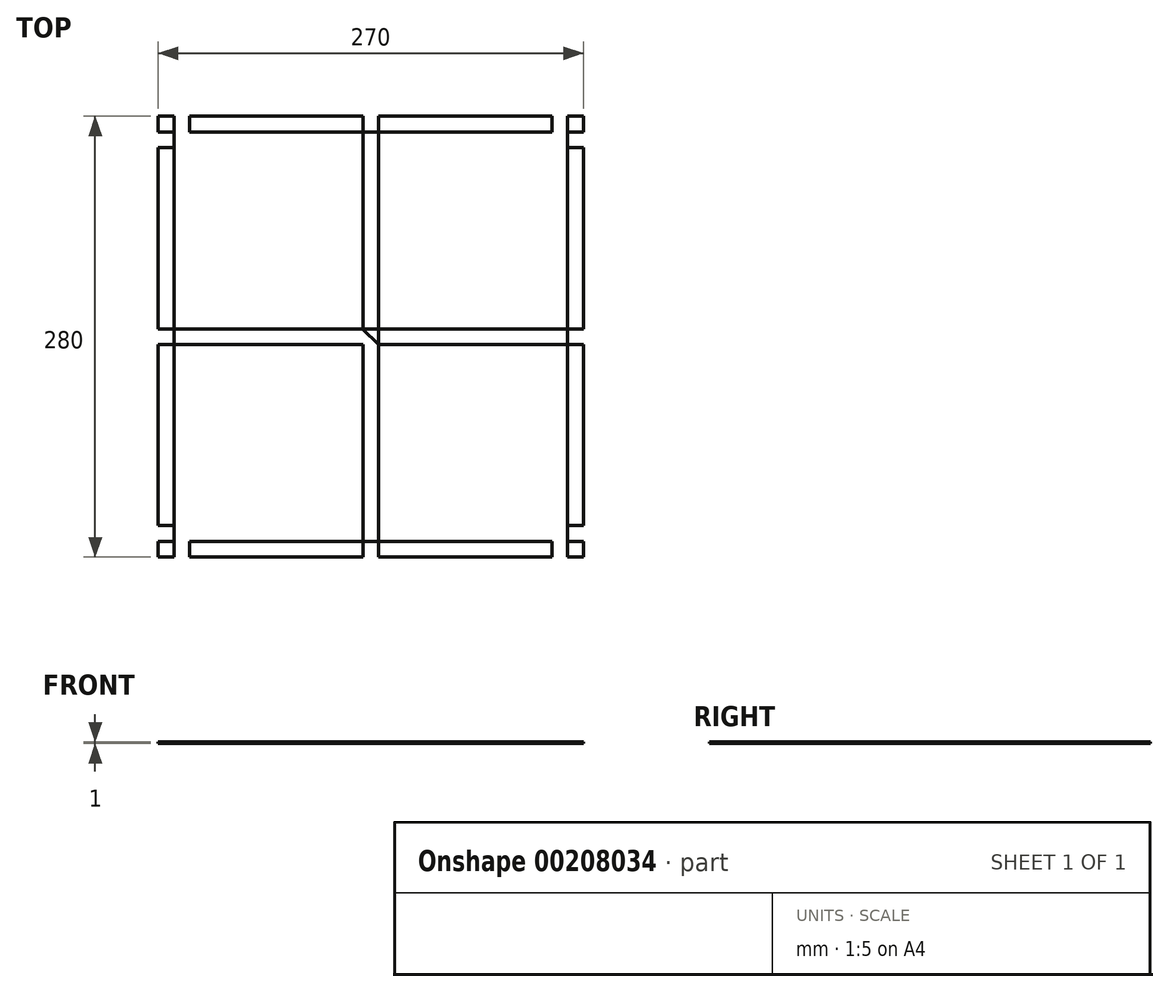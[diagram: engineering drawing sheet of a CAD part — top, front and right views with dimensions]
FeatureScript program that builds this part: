
annotation { "Feature Type Name" : "Feature", "Feature Type Description" : "" }
export const myFeature = defineFeature(function(context is Context, id is Id, definition is map)
    precondition{}
    {
        {
            var Q0;
            Q0=qCreatedBy(makeId("Top.planeOp"),FACE);
            var sketch = newSketch(context, id + "F0", { "sketchPlane" : qUnion([Q0])});
            skLineSegment(sketch, "E0.bottom", {"start": v(-135, 140) * mm, "end": v(135, 140) * mm});
            skLineSegment(sketch, "E0.top", {"start": v(-135, -140) * mm, "end": v(135, -140) * mm});
            skLineSegment(sketch, "E0.left", {"start": v(-135, 140) * mm, "end": v(-135, -140) * mm});
            skLineSegment(sketch, "E0.right", {"start": v(135, 140) * mm, "end": v(135, -140) * mm});
            skSolve(sketch);
        }
        {
            var Q0;
            Q0=makeQuery(id+"F0.imprint","IMPRINT",FACE,{"disambiguationData":[TD([[makeQuery(id+"F0.imprint","IMPRINT",EDGE,{"derivedFrom":sQuery(id+"F0.wireOp",EDGE,"E0.bottom")}),-1.0]])]});
            extrude(context, id + "F1", {"entities" : qUnion([Q0]), "depth" : 1 * mm});
        }
        {
            var Q0;
            Q0=makeQuery(id+"F1.opExtrude","CAP_FACE",FACE,{"disambiguationData":[OSD([sQuery(id+"F0.wireOp",EDGE,"E0.bottom"),sQuery(id+"F0.wireOp",EDGE,"E0.top"),sQuery(id+"F0.wireOp",EDGE,"E0.left"),sQuery(id+"F0.wireOp",EDGE,"E0.right")])],"isStart":false});
            var sketch = newSketch(context, id + "F2", { "sketchPlane" : qUnion([Q0])});
            skLineSegment(sketch, "E1.bottom", {"start": v(-125, 130) * mm, "end": v(-5, 130) * mm});
            skLineSegment(sketch, "E1.top", {"start": v(-125, 5) * mm, "end": v(-5, 5) * mm});
            skLineSegment(sketch, "E1.left", {"start": v(-125, 130) * mm, "end": v(-125, 5) * mm});
            skLineSegment(sketch, "E1.right", {"start": v(-5, 130) * mm, "end": v(-5, 5) * mm});
            skLineSegment(sketch, "E2.bottom", {"start": v(5, 130) * mm, "end": v(125, 130) * mm});
            skLineSegment(sketch, "E2.top", {"start": v(5, 5) * mm, "end": v(125, 5) * mm});
            skLineSegment(sketch, "E2.left", {"start": v(5, 130) * mm, "end": v(5, 5) * mm});
            skLineSegment(sketch, "E2.right", {"start": v(125, 130) * mm, "end": v(125, 5) * mm});
            skLineSegment(sketch, "E3.bottom", {"start": v(-125, -5) * mm, "end": v(-5, -5) * mm});
            skLineSegment(sketch, "E3.top", {"start": v(-125, -130) * mm, "end": v(-5, -130) * mm});
            skLineSegment(sketch, "E3.left", {"start": v(-125, -5) * mm, "end": v(-125, -130) * mm});
            skLineSegment(sketch, "E3.right", {"start": v(-5, -5) * mm, "end": v(-5, -130) * mm});
            skLineSegment(sketch, "E4.bottom", {"start": v(5, -5) * mm, "end": v(125, -5) * mm});
            skLineSegment(sketch, "E4.top", {"start": v(5, -130) * mm, "end": v(125, -130) * mm});
            skLineSegment(sketch, "E4.left", {"start": v(5, -5) * mm, "end": v(5, -130) * mm});
            skLineSegment(sketch, "E4.right", {"start": v(125, -5) * mm, "end": v(125, -130) * mm});
            skSolve(sketch);
        }
        {
            var Q0;
            Q0=makeQuery(id+"F2.imprint","IMPRINT",FACE,{"disambiguationData":[TD([[makeQuery(id+"F2.imprint","IMPRINT",EDGE,{"derivedFrom":sQuery(id+"F2.wireOp",EDGE,"E1.bottom")}),-1.0]])]});
            var Q1;
            Q1=makeQuery(id+"F2.imprint","IMPRINT",FACE,{"disambiguationData":[TD([[makeQuery(id+"F2.imprint","IMPRINT",EDGE,{"derivedFrom":sQuery(id+"F2.wireOp",EDGE,"E2.bottom")}),-1.0]])]});
            var Q2;
            Q2=makeQuery(id+"F2.imprint","IMPRINT",FACE,{"disambiguationData":[TD([[makeQuery(id+"F2.imprint","IMPRINT",EDGE,{"derivedFrom":sQuery(id+"F2.wireOp",EDGE,"E4.bottom")}),-1.0]])]});
            var Q3;
            Q3=makeQuery(id+"F2.imprint","IMPRINT",FACE,{"disambiguationData":[TD([[makeQuery(id+"F2.imprint","IMPRINT",EDGE,{"derivedFrom":sQuery(id+"F2.wireOp",EDGE,"E3.bottom")}),-1.0]])]});
            extrude(context, id + "F3", {"entities" : qUnion([Q0, Q1, Q2, Q3]), "operationType" : NewBodyOperationType.REMOVE, "endBound" : BoundingType.THROUGH_ALL, "oppositeDirection" : true, "depth" : 25 * mm});
        }
        {
            var Q0;
            Q0=makeQuery(id+"F2.imprint","IMPRINT",FACE,{"disambiguationData":[TD([[makeQuery(id+"F2.imprint","IMPRINT",EDGE,{"derivedFrom":sQuery(id+"F2.wireOp",EDGE,"E1.bottom")}),1.0]])]});
            var sketch = newSketch(context, id + "F4", { "sketchPlane" : qUnion([Q0])});
            skLineSegment(sketch, "E5.bottom", {"start": v(-125.01, 130) * mm, "end": v(-135.01, 130) * mm});
            skLineSegment(sketch, "E5.top", {"start": v(-125.01, 120) * mm, "end": v(-135.01, 120) * mm});
            skLineSegment(sketch, "E5.left", {"start": v(-125.01, 130) * mm, "end": v(-125.01, 120) * mm});
            skLineSegment(sketch, "E5.right", {"start": v(-135.01, 130) * mm, "end": v(-135.01, 120) * mm});
            skLineSegment(sketch, "E6.MirrorCS", {"start": v(125.01, 130) * mm, "end": v(125.01, 120) * mm});
            skLineSegment(sketch, "E7.MirrorCS", {"start": v(125.01, 130) * mm, "end": v(135.01, 130) * mm});
            skLineSegment(sketch, "E8.MirrorCS", {"start": v(125.01, 120) * mm, "end": v(135.01, 120) * mm});
            skLineSegment(sketch, "E9.MirrorCS", {"start": v(135.01, 130) * mm, "end": v(135.01, 120) * mm});
            skLineSegment(sketch, "E10.MirrorCS", {"start": v(-125.01, -130) * mm, "end": v(-135.01, -130) * mm});
            skLineSegment(sketch, "E11.MirrorCS", {"start": v(-135.01, -130) * mm, "end": v(-135.01, -120) * mm});
            skLineSegment(sketch, "E12.MirrorCS", {"start": v(-125.01, -130) * mm, "end": v(-125.01, -120) * mm});
            skLineSegment(sketch, "E13.MirrorCS", {"start": v(125.01, -130) * mm, "end": v(135.01, -130) * mm});
            skLineSegment(sketch, "E14.MirrorCS", {"start": v(135.01, -130) * mm, "end": v(135.01, -120) * mm});
            skLineSegment(sketch, "E15.MirrorCS", {"start": v(125.01, -130) * mm, "end": v(125.01, -120) * mm});
            skLineSegment(sketch, "E16.MirrorCS", {"start": v(125.01, -120) * mm, "end": v(135.01, -120) * mm});
            skLineSegment(sketch, "E17.MirrorCS", {"start": v(-125.01, -120) * mm, "end": v(-135.01, -120) * mm});
            skSolve(sketch);
        }
        {
            var Q0;
            Q0 = qSketchRegion(id + "F4", true);
            extrude(context, id + "F5", {"entities" : qUnion([Q0]), "operationType" : NewBodyOperationType.REMOVE, "endBound" : BoundingType.THROUGH_ALL, "oppositeDirection" : true, "depth" : 25 * mm});
        }
        {
            var Q0;
            Q0=makeQuery(id+"F2.imprint","IMPRINT",FACE,{"disambiguationData":[TD([[makeQuery(id+"F2.imprint","IMPRINT",EDGE,{"derivedFrom":sQuery(id+"F2.wireOp",EDGE,"E1.bottom")}),1.0]])]});
            var sketch = newSketch(context, id + "F6", { "sketchPlane" : qUnion([Q0])});
            skLineSegment(sketch, "E18.bottom", {"start": v(-125, 130) * mm, "end": v(-115, 130) * mm});
            skLineSegment(sketch, "E18.top", {"start": v(-125, 140) * mm, "end": v(-115, 140) * mm});
            skLineSegment(sketch, "E18.left", {"start": v(-125, 130) * mm, "end": v(-125, 140) * mm});
            skLineSegment(sketch, "E18.right", {"start": v(-115, 130) * mm, "end": v(-115, 140) * mm});
            skLineSegment(sketch, "E19.MirrorCS", {"start": v(125, 130) * mm, "end": v(125, 140) * mm});
            skLineSegment(sketch, "E20.MirrorCS", {"start": v(125, 140) * mm, "end": v(115, 140) * mm});
            skLineSegment(sketch, "E21.MirrorCS", {"start": v(115, 130) * mm, "end": v(115, 140) * mm});
            skLineSegment(sketch, "E22.MirrorCS", {"start": v(125, 130) * mm, "end": v(115, 130) * mm});
            skLineSegment(sketch, "E23.MirrorCS", {"start": v(-125, -130) * mm, "end": v(-125, -140) * mm});
            skLineSegment(sketch, "E24.MirrorCS", {"start": v(-125, -140) * mm, "end": v(-115, -140) * mm});
            skLineSegment(sketch, "E25.MirrorCS", {"start": v(-125, -130) * mm, "end": v(-115, -130) * mm});
            skLineSegment(sketch, "E26.MirrorCS", {"start": v(-115, -130) * mm, "end": v(-115, -140) * mm});
            skLineSegment(sketch, "E27.MirrorCS", {"start": v(115, -130) * mm, "end": v(115, -140) * mm});
            skLineSegment(sketch, "E28.MirrorCS", {"start": v(125, -140) * mm, "end": v(115, -140) * mm});
            skLineSegment(sketch, "E29.MirrorCS", {"start": v(125, -130) * mm, "end": v(125, -140) * mm});
            skLineSegment(sketch, "E30.MirrorCS", {"start": v(125, -130) * mm, "end": v(115, -130) * mm});
            skSolve(sketch);
        }
        {
            var Q0;
            Q0=makeQuery(id+"F6.imprint","IMPRINT",FACE,{"disambiguationData":[TD([[makeQuery(id+"F6.imprint","IMPRINT",EDGE,{"derivedFrom":sQuery(id+"F6.wireOp",EDGE,"E19.MirrorCS")}),1.0]])]});
            var Q1;
            Q1=makeQuery(id+"F6.imprint","IMPRINT",FACE,{"disambiguationData":[TD([[makeQuery(id+"F6.imprint","IMPRINT",EDGE,{"derivedFrom":sQuery(id+"F6.wireOp",EDGE,"E23.MirrorCS")}),1.0]])]});
            var Q2;
            Q2=makeQuery(id+"F6.imprint","IMPRINT",FACE,{"disambiguationData":[TD([[makeQuery(id+"F6.imprint","IMPRINT",EDGE,{"derivedFrom":sQuery(id+"F6.wireOp",EDGE,"E27.MirrorCS")}),1.0]])]});
            var Q3;
            Q3=makeQuery(id+"F6.imprint","IMPRINT",FACE,{"disambiguationData":[TD([[makeQuery(id+"F6.imprint","IMPRINT",EDGE,{"derivedFrom":sQuery(id+"F6.wireOp",EDGE,"E18.bottom")}),1.0]])]});
            extrude(context, id + "F7", {"entities" : qUnion([Q0, Q1, Q2, Q3]), "operationType" : NewBodyOperationType.REMOVE, "endBound" : BoundingType.THROUGH_ALL, "oppositeDirection" : true, "depth" : 25 * mm});
        }
        {
            var Q0;
            Q0=makeQuery(id+"F2.imprint","IMPRINT",FACE,{"disambiguationData":[TD([[makeQuery(id+"F2.imprint","IMPRINT",EDGE,{"derivedFrom":sQuery(id+"F2.wireOp",EDGE,"E1.bottom")}),1.0]])]});
            var sketch = newSketch(context, id + "F8", { "sketchPlane" : qUnion([Q0])});
            skLineSegment(sketch, "E31", {"start": v(-5.1, 5) * mm, "end": v(4.9, 5) * mm});
            skLineSegment(sketch, "E32", {"start": v(4.9, 5) * mm, "end": v(4.9, -5) * mm});
            skLineSegment(sketch, "E33", {"start": v(4.9, -5) * mm, "end": v(-5.1, 5) * mm});
            skSolve(sketch);
        }
        {
            var Q0;
            {var subQ0=sQuery(id+"F8.wireOp",EDGE,"E33");var subQ1=sQuery(id+"F8.wireOp",EDGE,"E31");var subQ2=makeQuery(id+"F8.imprint","INTERSECT",VERTEX,{"derivedFrom":[subQ1,subQ0]});Q0=makeQuery(id+"F8.imprint","IMPRINT",FACE,{"disambiguationData":[TD([[makeQuery(id+"F8.imprint","IMPRINT",EDGE,{"disambiguationData":[TD([[subQ2,-1.0]])],"derivedFrom":subQ1}),-1.0]])]});}
            var Q1;
            {var subQ0=sQuery(id+"F8.wireOp",EDGE,"E32");Q1=makeQuery(id+"F8.imprint","IMPRINT",FACE,{"disambiguationData":[TD([[makeQuery(id+"F8.imprint","IMPRINT",EDGE,{"derivedFrom":subQ0}),-1.0]])]});}
            extrude(context, id + "F9", {"entities" : qUnion([Q0, Q1]), "operationType" : NewBodyOperationType.REMOVE, "endBound" : BoundingType.THROUGH_ALL, "oppositeDirection" : true, "depth" : 25 * mm});
        }
        {
            var Q0;
            Q0=makeQuery(id+"F2.imprint","IMPRINT",FACE,{"disambiguationData":[TD([[makeQuery(id+"F2.imprint","IMPRINT",EDGE,{"derivedFrom":sQuery(id+"F2.wireOp",EDGE,"E1.bottom")}),1.0]])]});
            var sketch = newSketch(context, id + "F10", { "sketchPlane" : qUnion([Q0])});
            skLineSegment(sketch, "E34.bottom", {"start": v(-125, 5) * mm, "end": v(-135, 5) * mm});
            skLineSegment(sketch, "E34.top", {"start": v(-125, -5) * mm, "end": v(-135, -5) * mm});
            skLineSegment(sketch, "E34.left", {"start": v(-125, 5) * mm, "end": v(-125, -5) * mm});
            skLineSegment(sketch, "E34.right", {"start": v(-135, 5) * mm, "end": v(-135, -5) * mm});
            skLineSegment(sketch, "E35.MirrorCS", {"start": v(135, 5) * mm, "end": v(135, -5) * mm});
            skLineSegment(sketch, "E36.MirrorCS", {"start": v(125, 5) * mm, "end": v(135, 5) * mm});
            skLineSegment(sketch, "E37.MirrorCS", {"start": v(125, 5) * mm, "end": v(125, -5) * mm});
            skLineSegment(sketch, "E38.MirrorCS", {"start": v(125, -5) * mm, "end": v(135, -5) * mm});
            skSolve(sketch);
        }
        {
            var Q0;
            Q0 = qSketchRegion(id + "F10", true);
            extrude(context, id + "F11", {"entities" : qUnion([Q0]), "operationType" : NewBodyOperationType.REMOVE, "endBound" : BoundingType.THROUGH_ALL, "oppositeDirection" : true, "depth" : 25 * mm});
        }
        {
            var Q0;
            Q0=makeQuery(id+"F2.imprint","IMPRINT",FACE,{"disambiguationData":[TD([[makeQuery(id+"F2.imprint","IMPRINT",EDGE,{"derivedFrom":sQuery(id+"F2.wireOp",EDGE,"E1.bottom")}),1.0]])]});
            var sketch = newSketch(context, id + "F12", { "sketchPlane" : qUnion([Q0])});
            skLineSegment(sketch, "E39.bottom", {"start": v(-5, -130) * mm, "end": v(5, -130) * mm});
            skLineSegment(sketch, "E39.top", {"start": v(-5, -140) * mm, "end": v(5, -140) * mm});
            skLineSegment(sketch, "E39.left", {"start": v(-5, -130) * mm, "end": v(-5, -140) * mm});
            skLineSegment(sketch, "E39.right", {"start": v(5, -130) * mm, "end": v(5, -140) * mm});
            skLineSegment(sketch, "E40.MirrorCS", {"start": v(-5, 130) * mm, "end": v(5, 130) * mm});
            skLineSegment(sketch, "E41.MirrorCS", {"start": v(-5, 130) * mm, "end": v(-5, 140) * mm});
            skLineSegment(sketch, "E42.MirrorCS", {"start": v(-5, 140) * mm, "end": v(5, 140) * mm});
            skLineSegment(sketch, "E43.MirrorCS", {"start": v(5, 130) * mm, "end": v(5, 140) * mm});
            skSolve(sketch);
        }
        {
            var Q0;
            Q0 = qSketchRegion(id + "F12", true);
            extrude(context, id + "F13", {"entities" : qUnion([Q0]), "operationType" : NewBodyOperationType.REMOVE, "endBound" : BoundingType.THROUGH_ALL, "oppositeDirection" : true, "depth" : 25 * mm});
        }
    });
